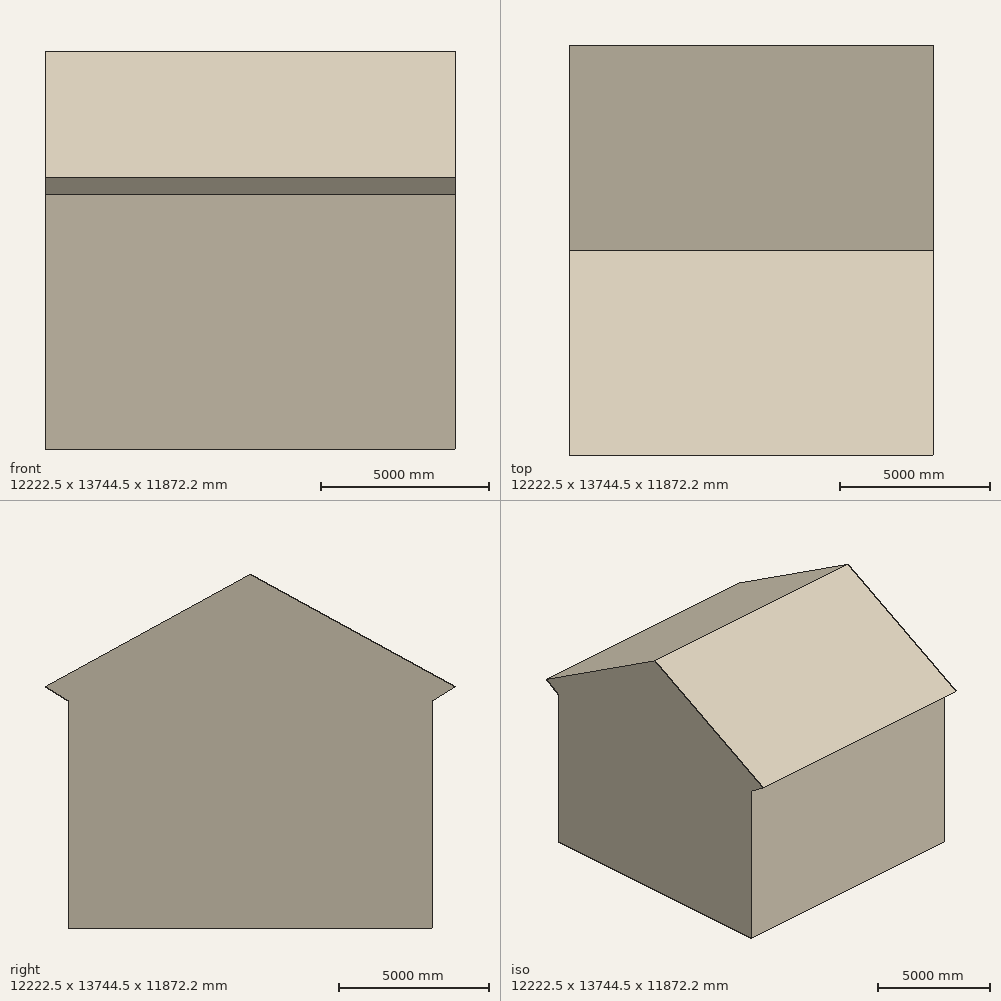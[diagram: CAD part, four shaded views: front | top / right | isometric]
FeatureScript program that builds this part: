
annotation { "Feature Type Name" : "Feature", "Feature Type Description" : "" }
export const myFeature = defineFeature(function(context is Context, id is Id, definition is map)
    precondition{}
    {
        {
            var Q0;
            Q0=qCreatedBy(makeId("Right.planeOp"),FACE);
            var sketch = newSketch(context, id + "F0", { "sketchPlane" : qUnion([Q0])});
            skLineSegment(sketch, "E0", {"start": v(0, 0) * mm, "end": v(-6096, 0) * mm});
            skLineSegment(sketch, "E1", {"start": v(0, 0) * mm, "end": v(6096, 0) * mm});
            skLineSegment(sketch, "E2", {"start": v(-6096, 0) * mm, "end": v(0, 3795.03) * mm});
            skLineSegment(sketch, "E3", {"start": v(0, 3795.03) * mm, "end": v(6096, 0) * mm});
            skLineSegment(sketch, "E4", {"start": v(-6096, 0) * mm, "end": v(-6096, -7315.2) * mm});
            skLineSegment(sketch, "E5", {"start": v(-6096, -7315.2) * mm, "end": v(6096, -7315.2) * mm});
            skLineSegment(sketch, "E6", {"start": v(6096, -7315.2) * mm, "end": v(6096, 0) * mm});
            skLineSegment(sketch, "E7", {"start": v(-6096, -7315.2) * mm, "end": v(-6096, -7620) * mm});
            skLineSegment(sketch, "E8", {"start": v(6096, -7315.2) * mm, "end": v(6096, -7620) * mm});
            skLineSegment(sketch, "E9", {"start": v(6096, -7620) * mm, "end": v(-6096, -7620) * mm});
            skLineSegment(sketch, "E10", {"start": v(0, -7315.2) * mm, "end": v(0, -5181.6) * mm});
            skLineSegment(sketch, "E11", {"start": v(0, -5181.6) * mm, "end": v(-914.4, -5181.6) * mm});
            skLineSegment(sketch, "E12", {"start": v(-914.4, -5181.6) * mm, "end": v(-914.4, -7315.2) * mm});
            skLineSegment(sketch, "E13", {"start": v(0, 3795.03) * mm, "end": v(0, 4252.23) * mm});
            skLineSegment(sketch, "E14", {"start": v(6096, 0) * mm, "end": v(6872.27, 483.26) * mm});
            skLineSegment(sketch, "E15", {"start": v(-6096, 0) * mm, "end": v(-6872.27, 483.26) * mm});
            skLineSegment(sketch, "E16", {"start": v(0, 4252.23) * mm, "end": v(-6872.27, 483.26) * mm});
            skLineSegment(sketch, "E17", {"start": v(0, 4252.23) * mm, "end": v(6872.27, 483.26) * mm});
            skLineSegment(sketch, "E18.bottom", {"start": v(-4267.2, -1219.2) * mm, "end": v(-2438.4, -1219.2) * mm});
            skLineSegment(sketch, "E18.top", {"start": v(-4267.2, -2438.4) * mm, "end": v(-2438.4, -2438.4) * mm});
            skLineSegment(sketch, "E18.left", {"start": v(-4267.2, -1219.2) * mm, "end": v(-4267.2, -2438.4) * mm});
            skLineSegment(sketch, "E18.right", {"start": v(-2438.4, -1219.2) * mm, "end": v(-2438.4, -2438.4) * mm});
            skLineSegment(sketch, "E19.bottom", {"start": v(2877.74, -1219.2) * mm, "end": v(4706.54, -1219.2) * mm});
            skLineSegment(sketch, "E19.top", {"start": v(2877.74, -2438.4) * mm, "end": v(4706.54, -2438.4) * mm});
            skLineSegment(sketch, "E19.left", {"start": v(2877.74, -1219.2) * mm, "end": v(2877.74, -2438.4) * mm});
            skLineSegment(sketch, "E19.right", {"start": v(4706.54, -1219.2) * mm, "end": v(4706.54, -2438.4) * mm});
            skSolve(sketch);
        }
        {
            var Q0;
            {var subQ0=sQuery(id+"F0.wireOp",EDGE,"E7");Q0=makeQuery(id+"F0.imprint","IMPRINT",FACE,{"disambiguationData":[TD([[makeQuery(id+"F0.imprint","IMPRINT",EDGE,{"derivedFrom":subQ0}),1.0]])]});}
            var Q1;
            {var subQ0=sQuery(id+"F0.wireOp",EDGE,"E10");Q1=makeQuery(id+"F0.imprint","IMPRINT",FACE,{"disambiguationData":[TD([[makeQuery(id+"F0.imprint","IMPRINT",EDGE,{"derivedFrom":subQ0}),1.0]])]});}
            var Q2;
            Q2=makeQuery(id+"F0.imprint","IMPRINT",FACE,{"disambiguationData":[TD([[makeQuery(id+"F0.imprint","IMPRINT",EDGE,{"derivedFrom":sQuery(id+"F0.wireOp",EDGE,"E19.bottom")}),-1.0]])]});
            var Q3;
            Q3=makeQuery(id+"F0.imprint","IMPRINT",FACE,{"disambiguationData":[TD([[makeQuery(id+"F0.imprint","IMPRINT",EDGE,{"derivedFrom":sQuery(id+"F0.wireOp",EDGE,"E0")}),-1.0]])]});
            var Q4;
            Q4=makeQuery(id+"F0.imprint","IMPRINT",FACE,{"disambiguationData":[TD([[makeQuery(id+"F0.imprint","IMPRINT",EDGE,{"derivedFrom":sQuery(id+"F0.wireOp",EDGE,"E0")}),1.0]])]});
            var Q5;
            Q5=makeQuery(id+"F0.imprint","IMPRINT",FACE,{"disambiguationData":[TD([[makeQuery(id+"F0.imprint","IMPRINT",EDGE,{"derivedFrom":sQuery(id+"F0.wireOp",EDGE,"E3")}),1.0]])]});
            var Q6;
            Q6=makeQuery(id+"F0.imprint","IMPRINT",FACE,{"disambiguationData":[TD([[makeQuery(id+"F0.imprint","IMPRINT",EDGE,{"derivedFrom":sQuery(id+"F0.wireOp",EDGE,"E18.bottom")}),-1.0]])]});
            var Q7;
            Q7=makeQuery(id+"F0.imprint","IMPRINT",FACE,{"disambiguationData":[TD([[makeQuery(id+"F0.imprint","IMPRINT",EDGE,{"derivedFrom":sQuery(id+"F0.wireOp",EDGE,"E2")}),1.0]])]});
            extrude(context, id + "F1", {"entities" : qUnion([Q0, Q1, Q2, Q3, Q4, Q5, Q6, Q7]), "depth" : 12192 * mm, "offsetDistance" : 30.48 * mm});
        }
        {
            var Q0;
            Q0=makeQuery(id+"F1.opExtrude","CAP_FACE",FACE,{"disambiguationData":[OSD([sQuery(id+"F0.wireOp",EDGE,"E4"),sQuery(id+"F0.wireOp",EDGE,"E6"),sQuery(id+"F0.wireOp",EDGE,"E7"),sQuery(id+"F0.wireOp",EDGE,"E8"),sQuery(id+"F0.wireOp",EDGE,"E9"),sQuery(id+"F0.wireOp",EDGE,"E14"),sQuery(id+"F0.wireOp",EDGE,"E15"),sQuery(id+"F0.wireOp",EDGE,"E16"),sQuery(id+"F0.wireOp",EDGE,"E17")])],"isStart":false});
            var Q1;
            Q1=makeQuery(id+"F1.opExtrude","CAP_FACE",FACE,{"disambiguationData":[OSD([sQuery(id+"F0.wireOp",EDGE,"E4"),sQuery(id+"F0.wireOp",EDGE,"E6"),sQuery(id+"F0.wireOp",EDGE,"E7"),sQuery(id+"F0.wireOp",EDGE,"E8"),sQuery(id+"F0.wireOp",EDGE,"E9"),sQuery(id+"F0.wireOp",EDGE,"E14"),sQuery(id+"F0.wireOp",EDGE,"E15"),sQuery(id+"F0.wireOp",EDGE,"E16"),sQuery(id+"F0.wireOp",EDGE,"E17")])],"isStart":true});
            extrude(context, id + "F2", {"entities" : qUnion([Q0, Q1]), "operationType" : NewBodyOperationType.ADD, "depth" : 30.48 * mm, "offsetDistance" : 30.48 * mm});
        }
    });
